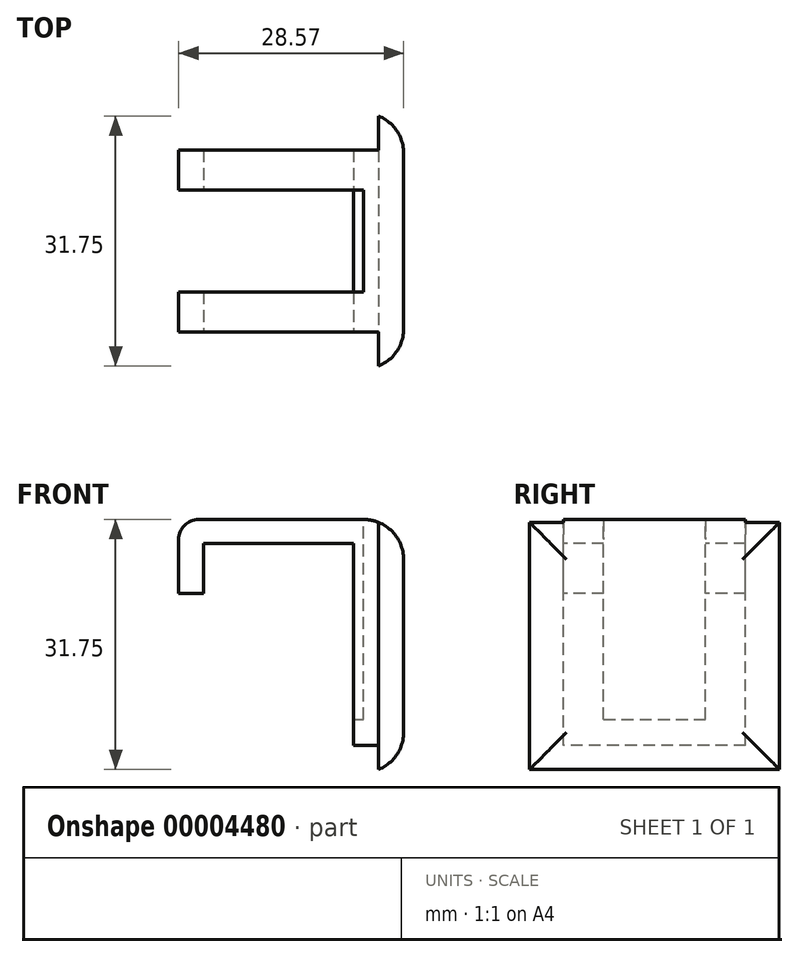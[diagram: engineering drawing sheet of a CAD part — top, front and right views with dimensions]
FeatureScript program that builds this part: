
annotation { "Feature Type Name" : "Feature", "Feature Type Description" : "" }
export const myFeature = defineFeature(function(context is Context, id is Id, definition is map)
    precondition{}
    {
        {
            var Q0;
            Q0=qCreatedBy(makeId("Right.planeOp"),FACE);
            var sketch = newSketch(context, id + "F0", { "sketchPlane" : qUnion([Q0])});
            skLineSegment(sketch, "E0.bottom", {"start": v(-24.37, 22.63) * mm, "end": v(7.38, 22.63) * mm});
            skLineSegment(sketch, "E0.top", {"start": v(-24.37, -9.12) * mm, "end": v(7.38, -9.12) * mm});
            skLineSegment(sketch, "E0.left", {"start": v(-24.37, 22.63) * mm, "end": v(-24.37, -9.12) * mm});
            skLineSegment(sketch, "E0.right", {"start": v(7.38, 22.63) * mm, "end": v(7.38, -9.12) * mm});
            skSolve(sketch);
        }
        {
            var Q0;
            Q0=makeQuery(id+"F0.imprint","IMPRINT",FACE,{"disambiguationData":[TD([[makeQuery(id+"F0.imprint","IMPRINT",EDGE,{"derivedFrom":sQuery(id+"F0.wireOp",EDGE,"E0.bottom")}),-1.0]])]});
            extrude(context, id + "F1", {"entities" : qUnion([Q0]), "depth" : 3.17 * mm});
        }
        {
            var Q0;
            Q0=makeQuery(id+"F1.opExtrude","CAP_FACE",FACE,{"disambiguationData":[OSD([sQuery(id+"F0.wireOp",EDGE,"E0.bottom"),sQuery(id+"F0.wireOp",EDGE,"E0.top"),sQuery(id+"F0.wireOp",EDGE,"E0.left"),sQuery(id+"F0.wireOp",EDGE,"E0.right")])],"isStart":true});
            var sketch = newSketch(context, id + "F2", { "sketchPlane" : qUnion([Q0])});
            skLineSegment(sketch, "E1.bottom", {"start": v(-7.38, 22.63) * mm, "end": v(24.37, 22.63) * mm});
            skLineSegment(sketch, "E1.top", {"start": v(-7.38, -9.12) * mm, "end": v(24.37, -9.12) * mm});
            skLineSegment(sketch, "E1.left", {"start": v(-7.38, 22.63) * mm, "end": v(-7.38, -9.12) * mm});
            skLineSegment(sketch, "E1.right", {"start": v(24.37, 22.63) * mm, "end": v(24.37, -9.12) * mm});
            skLineSegment(sketch, "E2.0", {"start": v(-4.34, 19.58) * mm, "end": v(21.32, 19.58) * mm});
            skLineSegment(sketch, "E2.1", {"start": v(-4.34, 19.58) * mm, "end": v(-4.34, -6.07) * mm});
            skLineSegment(sketch, "E2.2", {"start": v(-4.34, -6.07) * mm, "end": v(21.32, -6.07) * mm});
            skLineSegment(sketch, "E2.3", {"start": v(21.32, 19.58) * mm, "end": v(21.32, -6.07) * mm});
            skSolve(sketch);
        }
        {
            var Q0;
            Q0=makeQuery(id+"F2.imprint","IMPRINT",FACE,{"disambiguationData":[TD([[makeQuery(id+"F2.imprint","IMPRINT",EDGE,{"derivedFrom":sQuery(id+"F2.wireOp",EDGE,"E2.0")}),-1.0]])]});
            extrude(context, id + "F3", {"entities" : qUnion([Q0]), "operationType" : NewBodyOperationType.ADD, "depth" : 3.17 * mm});
        }
        {
            var Q0;
            Q0=makeQuery(id+"F1.opExtrude","CAP_FACE",FACE,{"disambiguationData":[OSD([sQuery(id+"F0.wireOp",EDGE,"E0.bottom"),sQuery(id+"F0.wireOp",EDGE,"E0.top"),sQuery(id+"F0.wireOp",EDGE,"E0.left"),sQuery(id+"F0.wireOp",EDGE,"E0.right")])],"isStart":true});
            var sketch = newSketch(context, id + "F4", { "sketchPlane" : qUnion([Q0])});
            skLineSegment(sketch, "E3.bottom", {"start": v(-4.34, 19.58) * mm, "end": v(21.32, 19.58) * mm});
            skLineSegment(sketch, "E3.top", {"start": v(-4.34, 22.63) * mm, "end": v(21.32, 22.63) * mm});
            skLineSegment(sketch, "E3.left", {"start": v(-4.34, 19.58) * mm, "end": v(-4.34, 22.63) * mm});
            skLineSegment(sketch, "E3.right", {"start": v(21.32, 19.58) * mm, "end": v(21.32, 22.63) * mm});
            skSolve(sketch);
        }
        {
            var Q0;
            Q0=makeQuery(id+"F4.imprint","IMPRINT",FACE,{"disambiguationData":[TD([[makeQuery(id+"F4.imprint","IMPRINT",EDGE,{"derivedFrom":sQuery(id+"F4.wireOp",EDGE,"E3.bottom")}),1.0]])]});
            extrude(context, id + "F5", {"entities" : qUnion([Q0]), "operationType" : NewBodyOperationType.ADD, "depth" : 25.4 * mm});
        }
        {
            var Q0;
            Q0=makeQuery(id+"F5.opExtrude","SWEPT_FACE",FACE,{"disambiguationData":[OSD([sQuery(id+"F4.wireOp",EDGE,"E3.bottom")])]});
            var sketch = newSketch(context, id + "F6", { "sketchPlane" : qUnion([Q0])});
            skLineSegment(sketch, "E4.bottom", {"start": v(-25.4, -4.34) * mm, "end": v(-22.22, -4.34) * mm});
            skLineSegment(sketch, "E4.top", {"start": v(-25.4, 21.32) * mm, "end": v(-22.23, 21.32) * mm});
            skLineSegment(sketch, "E4.left", {"start": v(-25.4, -4.34) * mm, "end": v(-25.4, 21.32) * mm});
            skLineSegment(sketch, "E4.right", {"start": v(-22.22, -4.34) * mm, "end": v(-22.23, 21.32) * mm});
            skSolve(sketch);
        }
        {
            var Q0;
            Q0=makeQuery(id+"F6.imprint","IMPRINT",FACE,{"disambiguationData":[TD([[makeQuery(id+"F6.imprint","IMPRINT",EDGE,{"derivedFrom":sQuery(id+"F6.wireOp",EDGE,"E4.bottom")}),1.0]])]});
            extrude(context, id + "F7", {"entities" : qUnion([Q0]), "operationType" : NewBodyOperationType.ADD, "depth" : 6.35 * mm});
        }
        {
            var Q0;
            Q0=makeQuery(id+"F7.boolean.opBoolean","MERGE",FACE,{"derivedFrom":[makeQuery(id+"F5.opExtrude","CAP_FACE",FACE,{"disambiguationData":[OSD([sQuery(id+"F4.wireOp",EDGE,"E3.bottom"),sQuery(id+"F4.wireOp",EDGE,"E3.top"),sQuery(id+"F4.wireOp",EDGE,"E3.left"),sQuery(id+"F4.wireOp",EDGE,"E3.right")])],"isStart":false}),makeQuery(id+"F7.opExtrude","SWEPT_FACE",FACE,{"disambiguationData":[OSD([sQuery(id+"F6.wireOp",EDGE,"E4.left")])]})]});
            var sketch = newSketch(context, id + "F8", { "sketchPlane" : qUnion([Q0])});
            skLineSegment(sketch, "E5", {"start": v(-4.34, 13.23) * mm, "end": v(2.01, 13.23) * mm});
            skLineSegment(sketch, "E6", {"start": v(21.32, 13.23) * mm, "end": v(14.97, 13.23) * mm});
            skLineSegment(sketch, "E7.bottom", {"start": v(2.01, 13.23) * mm, "end": v(14.97, 13.23) * mm});
            skLineSegment(sketch, "E7.top", {"start": v(2.01, 22.63) * mm, "end": v(14.97, 22.63) * mm});
            skLineSegment(sketch, "E7.left", {"start": v(2.01, 13.23) * mm, "end": v(2.01, 22.63) * mm});
            skLineSegment(sketch, "E7.right", {"start": v(14.97, 13.23) * mm, "end": v(14.97, 22.63) * mm});
            skSolve(sketch);
        }
        {
            var Q0;
            Q0=makeQuery(id+"F8.imprint","IMPRINT",FACE,{"disambiguationData":[TD([[makeQuery(id+"F8.imprint","IMPRINT",EDGE,{"derivedFrom":sQuery(id+"F8.wireOp",EDGE,"E7.bottom")}),1.0]])]});
            extrude(context, id + "F9", {"entities" : qUnion([Q0]), "operationType" : NewBodyOperationType.REMOVE, "oppositeDirection" : true, "depth" : 19.05 * mm});
        }
        {
            var Q0;
            Q0=makeQuery(id+"F1.opExtrude","CAP_EDGE",EDGE,{"disambiguationData":[OSD([sQuery(id+"F0.wireOp",EDGE,"E0.bottom")])],"isStart":false});
            var Q1;
            Q1=makeQuery(id+"F1.opExtrude","CAP_EDGE",EDGE,{"disambiguationData":[OSD([sQuery(id+"F0.wireOp",EDGE,"E0.left")])],"isStart":false});
            var Q2;
            Q2=makeQuery(id+"F1.opExtrude","CAP_EDGE",EDGE,{"disambiguationData":[OSD([sQuery(id+"F0.wireOp",EDGE,"E0.top")])],"isStart":false});
            var Q3;
            Q3=makeQuery(id+"F1.opExtrude","CAP_EDGE",EDGE,{"disambiguationData":[OSD([sQuery(id+"F0.wireOp",EDGE,"E0.right")])],"isStart":false});
            fillet(context, id + "F10", {"entities" : qUnion([Q0, Q1, Q2, Q3]), "radius" : 5.08 * mm, "tangentPropagation" : true, "allowEdgeOverflow" : false});
        }
        {
            var Q0;
            Q0=makeQuery(id+"F5.boolean.opBoolean","MERGE",FACE,{"derivedFrom":[makeQuery(id+"F1.opExtrude","SWEPT_FACE",FACE,{"disambiguationData":[OSD([sQuery(id+"F0.wireOp",EDGE,"E0.bottom")])]}),makeQuery(id+"F5.opExtrude","SWEPT_FACE",FACE,{"disambiguationData":[OSD([sQuery(id+"F4.wireOp",EDGE,"E3.top")])]})]});
            var sketch = newSketch(context, id + "F11", { "sketchPlane" : qUnion([Q0])});
            skLineSegment(sketch, "E8.bottom", {"start": v(-25.4, 4.34) * mm, "end": v(0.04, 4.34) * mm});
            skLineSegment(sketch, "E8.top", {"start": v(-25.4, -21.32) * mm, "end": v(0.04, -21.32) * mm});
            skLineSegment(sketch, "E8.left", {"start": v(-25.4, 4.34) * mm, "end": v(-25.4, -21.32) * mm});
            skLineSegment(sketch, "E8.right", {"start": v(0.04, 4.34) * mm, "end": v(0.04, -21.32) * mm});
            skLineSegment(sketch, "E9", {"start": v(-25.4, 3.07) * mm, "end": v(0.04, 3.07) * mm});
            skLineSegment(sketch, "E10.0.MirrorCS", {"start": v(-25.4, -20.05) * mm, "end": v(0.04, -20.05) * mm});
            skSolve(sketch);
        }
        {
            var Q0;
            {var subQ2=sQuery(id+"F11.wireOp",EDGE,"E9");var subQ4=sQuery(id+"F11.wireOp",EDGE,"E8.bottom");var subQ6=sQuery(id+"F11.wireOp",EDGE,"E8.left");var subQ7=makeQuery(id+"F11.imprint","INTERSECT",VERTEX,{"derivedFrom":[subQ6,subQ2]});var subQ8=makeQuery(id+"F11.imprint","INTERSECT",VERTEX,{"derivedFrom":[subQ4,subQ6]});Q0=makeQuery(id+"F11.imprint","IMPRINT",FACE,{"disambiguationData":[TD([[makeQuery(id+"F11.imprint","IMPRINT",EDGE,{"disambiguationData":[TD([[subQ8,1.0],[subQ7,-1.0]])],"derivedFrom":subQ6}),-1.0]])]});}
            var Q1;
            {var subQ2=sQuery(id+"F11.wireOp",EDGE,"E10.0.MirrorCS");var subQ4=sQuery(id+"F11.wireOp",EDGE,"E8.top");var subQ6=sQuery(id+"F11.wireOp",EDGE,"E8.left");var subQ7=makeQuery(id+"F11.imprint","INTERSECT",VERTEX,{"derivedFrom":[subQ6,subQ2]});var subQ8=makeQuery(id+"F11.imprint","INTERSECT",VERTEX,{"derivedFrom":[subQ4,subQ6]});Q1=makeQuery(id+"F11.imprint","IMPRINT",FACE,{"disambiguationData":[TD([[makeQuery(id+"F11.imprint","IMPRINT",EDGE,{"disambiguationData":[TD([[subQ8,-1.0],[subQ7,1.0]])],"derivedFrom":subQ6}),-1.0]])]});}
            extrude(context, id + "F12", {"entities" : qUnion([Q0, Q1]), "operationType" : NewBodyOperationType.REMOVE, "oppositeDirection" : true, "depth" : 50.8 * mm});
        }
        {
            var Q0;
            {var subQ0=sQuery(id+"F0.wireOp",EDGE,"E0.bottom");var subQ1=sQuery(id+"F4.wireOp",EDGE,"E3.top");var subQ2=makeQuery(id+"F10.opFillet","BLEND_EDGE",EDGE,{"blendedFrom":[makeQuery(id+"F1.opExtrude","CAP_EDGE",EDGE,{"disambiguationData":[OSD([subQ0])],"isStart":false}),makeQuery(id+"F5.boolean.opBoolean","MERGE",FACE,{"derivedFrom":[makeQuery(id+"F1.opExtrude","SWEPT_FACE",FACE,{"disambiguationData":[OSD([subQ0])]}),makeQuery(id+"F5.opExtrude","SWEPT_FACE",FACE,{"disambiguationData":[OSD([subQ1])]})]})],"blendedInto":[makeQuery(id+"F5.boolean.opBoolean","MERGE",FACE,{"derivedFrom":[makeQuery(id+"F1.opExtrude","SWEPT_FACE",FACE,{"disambiguationData":[OSD([subQ0])]}),makeQuery(id+"F5.opExtrude","SWEPT_FACE",FACE,{"disambiguationData":[OSD([subQ1])]})]})]});Q0=makeQuery(id+"F12.boolean.opBoolean","COPY",FACE,{"derivedFrom":makeQuery(id+"F12.opExtrude","SWEPT_FACE",FACE,{"disambiguationData":[OSD([subQ0,subQ1]),TDD([makeQuery(id+"F11.imprint","IMPRINT",EDGE,{"disambiguationData":[TD([[makeQuery(id+"F11.imprint","INTERSECT",VERTEX,{"derivedFrom":[subQ2,sQuery(id+"F11.wireOp",EDGE,"E8.bottom")]}),1.0]])],"derivedFrom":subQ2})])]})});}
            var sketch = newSketch(context, id + "F13", { "sketchPlane" : qUnion([Q0])});
            skLineSegment(sketch, "E11.bottom", {"start": v(-3.07, 22.63) * mm, "end": v(-4.34, 22.63) * mm});
            skLineSegment(sketch, "E11.top", {"start": v(-3.07, -6.07) * mm, "end": v(-4.34, -6.07) * mm});
            skLineSegment(sketch, "E11.left", {"start": v(-3.07, 22.63) * mm, "end": v(-3.07, -6.07) * mm});
            skLineSegment(sketch, "E11.right", {"start": v(-4.34, 22.63) * mm, "end": v(-4.34, -6.07) * mm});
            skSolve(sketch);
        }
        {
            var Q0;
            Q0=makeQuery(id+"F13.imprint","IMPRINT",FACE,{"disambiguationData":[TD([[makeQuery(id+"F13.imprint","IMPRINT",EDGE,{"derivedFrom":sQuery(id+"F13.wireOp",EDGE,"E11.bottom")}),1.0]])]});
            extrude(context, id + "F14", {"entities" : qUnion([Q0]), "operationType" : NewBodyOperationType.REMOVE, "oppositeDirection" : true, "depth" : 1.9 * mm});
        }
        {
            var Q0;
            {var subQ0=sQuery(id+"F0.wireOp",EDGE,"E0.bottom");var subQ1=sQuery(id+"F4.wireOp",EDGE,"E3.top");var subQ2=makeQuery(id+"F10.opFillet","BLEND_EDGE",EDGE,{"blendedFrom":[makeQuery(id+"F1.opExtrude","CAP_EDGE",EDGE,{"disambiguationData":[OSD([subQ0])],"isStart":false}),makeQuery(id+"F5.boolean.opBoolean","MERGE",FACE,{"derivedFrom":[makeQuery(id+"F1.opExtrude","SWEPT_FACE",FACE,{"disambiguationData":[OSD([subQ0])]}),makeQuery(id+"F5.opExtrude","SWEPT_FACE",FACE,{"disambiguationData":[OSD([subQ1])]})]})],"blendedInto":[makeQuery(id+"F5.boolean.opBoolean","MERGE",FACE,{"derivedFrom":[makeQuery(id+"F1.opExtrude","SWEPT_FACE",FACE,{"disambiguationData":[OSD([subQ0])]}),makeQuery(id+"F5.opExtrude","SWEPT_FACE",FACE,{"disambiguationData":[OSD([subQ1])]})]})]});Q0=makeQuery(id+"F12.boolean.opBoolean","COPY",FACE,{"derivedFrom":makeQuery(id+"F12.opExtrude","SWEPT_FACE",FACE,{"disambiguationData":[OSD([subQ0,subQ1]),TDD([makeQuery(id+"F11.imprint","IMPRINT",EDGE,{"disambiguationData":[TD([[makeQuery(id+"F11.imprint","INTERSECT",VERTEX,{"derivedFrom":[subQ2,sQuery(id+"F11.wireOp",EDGE,"E8.top")]}),-1.0]])],"derivedFrom":subQ2})])]})});}
            var sketch = newSketch(context, id + "F15", { "sketchPlane" : qUnion([Q0])});
            skLineSegment(sketch, "E12.bottom", {"start": v(21.32, 22.63) * mm, "end": v(20.05, 22.63) * mm});
            skLineSegment(sketch, "E12.top", {"start": v(21.32, -6.07) * mm, "end": v(20.05, -6.07) * mm});
            skLineSegment(sketch, "E12.left", {"start": v(21.32, 22.63) * mm, "end": v(21.32, -6.07) * mm});
            skLineSegment(sketch, "E12.right", {"start": v(20.05, 22.63) * mm, "end": v(20.05, -6.07) * mm});
            skSolve(sketch);
        }
        {
            var Q0;
            Q0=makeQuery(id+"F15.imprint","IMPRINT",FACE,{"disambiguationData":[TD([[makeQuery(id+"F15.imprint","IMPRINT",EDGE,{"derivedFrom":sQuery(id+"F15.wireOp",EDGE,"E12.bottom")}),1.0]])]});
            extrude(context, id + "F16", {"entities" : qUnion([Q0]), "operationType" : NewBodyOperationType.REMOVE, "oppositeDirection" : true, "depth" : 1.9 * mm});
        }
        {
            var Q0;
            {var subQ0=sQuery(id+"F4.wireOp",EDGE,"E3.top");Q0=makeQuery(id+"F9.boolean.opBoolean","SPLIT",EDGE,{"disambiguationData":[TD([makeQuery(id+"F3.opExtrude","SWEPT_FACE",FACE,{"disambiguationData":[OSD([sQuery(id+"F2.wireOp",EDGE,"E2.3")])]})])],"derivedFrom":makeQuery(id+"F5.opExtrude","CAP_EDGE",EDGE,{"disambiguationData":[OSD([subQ0])],"isStart":false})});}
            var Q1;
            {var subQ0=sQuery(id+"F4.wireOp",EDGE,"E3.top");Q1=makeQuery(id+"F9.boolean.opBoolean","SPLIT",EDGE,{"disambiguationData":[TD([makeQuery(id+"F3.opExtrude","SWEPT_FACE",FACE,{"disambiguationData":[OSD([sQuery(id+"F2.wireOp",EDGE,"E2.1")])]})])],"derivedFrom":makeQuery(id+"F5.opExtrude","CAP_EDGE",EDGE,{"disambiguationData":[OSD([subQ0])],"isStart":false})});}
            fillet(context, id + "F17", {"entities" : qUnion([Q0, Q1]), "radius" : 2.54 * mm, "tangentPropagation" : true, "allowEdgeOverflow" : false});
        }
        {
            var Q0;
            Q0=makeQuery(id+"F3.opExtrude","CAP_FACE",FACE,{"disambiguationData":[OSD([sQuery(id+"F2.wireOp",EDGE,"E2.0"),sQuery(id+"F2.wireOp",EDGE,"E2.1"),sQuery(id+"F2.wireOp",EDGE,"E2.2"),sQuery(id+"F2.wireOp",EDGE,"E2.3")])],"isStart":false});
            var sketch = newSketch(context, id + "F18", { "sketchPlane" : qUnion([Q0])});
            skLineSegment(sketch, "E13.bottom", {"start": v(20.05, -6.07) * mm, "end": v(-3.07, -6.07) * mm});
            skLineSegment(sketch, "E13.top", {"start": v(20.05, 19.58) * mm, "end": v(-3.07, 19.58) * mm});
            skLineSegment(sketch, "E13.left", {"start": v(20.05, -6.07) * mm, "end": v(20.05, 19.58) * mm});
            skLineSegment(sketch, "E13.right", {"start": v(-3.07, -6.07) * mm, "end": v(-3.07, 19.58) * mm});
            skSolve(sketch);
        }
        {
            var Q0;
            Q0=makeQuery(id+"F18.imprint","IMPRINT",FACE,{"disambiguationData":[TD([[makeQuery(id+"F18.imprint","IMPRINT",EDGE,{"derivedFrom":sQuery(id+"F18.wireOp",EDGE,"E13.bottom")}),1.0]])]});
            extrude(context, id + "F19", {"entities" : qUnion([Q0]), "operationType" : NewBodyOperationType.REMOVE, "oppositeDirection" : true, "depth" : 1 / 203.2 * mm});
        }
        {
            var Q0;
            Q0=makeQuery(id+"F5.boolean.opBoolean","MERGE",FACE,{"derivedFrom":[makeQuery(id+"F1.opExtrude","SWEPT_FACE",FACE,{"disambiguationData":[OSD([sQuery(id+"F0.wireOp",EDGE,"E0.bottom")])]}),makeQuery(id+"F5.opExtrude","SWEPT_FACE",FACE,{"disambiguationData":[OSD([sQuery(id+"F4.wireOp",EDGE,"E3.top")])]})]});
            var sketch = newSketch(context, id + "F20", { "sketchPlane" : qUnion([Q0])});
            skLineSegment(sketch, "E14.bottom", {"start": v(-6.35, -14.97) * mm, "end": v(-1.9, -14.97) * mm});
            skLineSegment(sketch, "E14.top", {"start": v(-6.35, -2.01) * mm, "end": v(-1.9, -2.01) * mm});
            skLineSegment(sketch, "E14.left", {"start": v(-6.35, -14.97) * mm, "end": v(-6.35, -2.01) * mm});
            skLineSegment(sketch, "E14.right", {"start": v(-1.9, -14.97) * mm, "end": v(-1.9, -2.01) * mm});
            skSolve(sketch);
        }
        {
            var Q0;
            Q0=makeQuery(id+"F20.imprint","IMPRINT",FACE,{"disambiguationData":[TD([[makeQuery(id+"F20.imprint","IMPRINT",EDGE,{"derivedFrom":sQuery(id+"F20.wireOp",EDGE,"E14.bottom")}),1.0]])]});
            extrude(context, id + "F21", {"entities" : qUnion([Q0]), "operationType" : NewBodyOperationType.REMOVE, "oppositeDirection" : true, "depth" : 25.4 * mm});
        }
    });
